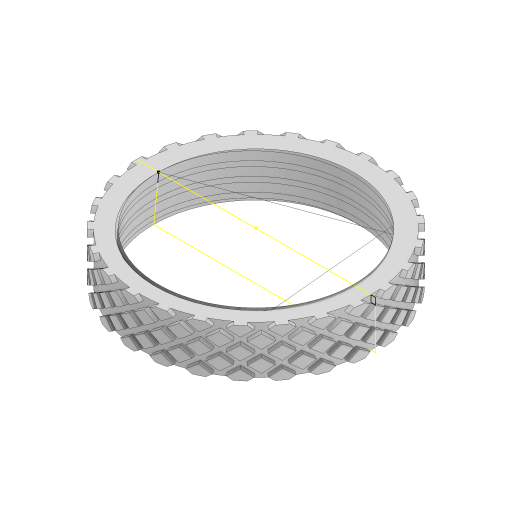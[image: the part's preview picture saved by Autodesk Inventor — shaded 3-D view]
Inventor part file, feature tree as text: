
AUTODESK INVENTOR PART (.ipt)
format: ipt  version: 2023 (Build 270158000, 158)  size: 1,646,592 bytes
history: native  units: mm
features: helix x6, sketch x4, pattern_circular x2, extrude x1, draft x1
ambient origin geometry x8: Origin, YZ Plane, XZ Plane, XY Plane, X Axis, Y Axis, Z Axis, Center Point
bodies: Solid1 (feature_tree)
feature tree (14):
  extrude  "Extrusion1"  Depth=6.52mm TaperAngle=0.0deg
  draft  "FaceDraft1"
  sketch  "Sketch2"  dims[d7=2.0mm d8=9.0mm d9=10.0mm d10=1.047198mm d11=90.0deg d12=90.0deg d13=0.0mm d14=0.0mm d15=2.0mm d16=3.0mm d17=10.0mm d18=-1.047198mm d19=90.0deg d20=90.0deg d21=0.0mm d22=0.0mm d23=3.0mm]
  sketch  "Sketch4"  dims[d52=70.0mm d53=9.0mm d54=10.0mm d55=0.0mm d56=90.0deg d57=90.0deg d58=0.0mm d59=0.0mm d60=70.0mm d61=9.0mm d62=10.0mm d63=0.0mm d64=90.0deg d65=90.0deg d66=0.0mm d67=0.0mm d68=250.0mm d69=360.0deg]
  helix  "Coil1"  [1 undecoded]
  helix  "Coil2"  [1 undecoded]
  sketch  "Sketch7"  dims[d71=70.0mm d72=9.0mm d73=10.0mm d74=0.0mm d75=90.0deg d76=90.0deg d77=0.0mm d78=0.0mm d79=70.0mm d80=9.0mm d81=10.0mm d82=0.0mm d83=90.0deg d84=90.0deg d85=0.0mm d86=0.0mm d87=250.0mm d88=360.0deg]
  helix  "Coil6"  [1 undecoded]
  helix  "Coil7"  [1 undecoded]
  pattern_circular  "Circular Pattern1"  [2 undecoded]
  helix  "Coil8"  [1 undecoded]
  helix  "Coil9"  [1 undecoded]
  pattern_circular  "Circular Pattern2"  [2 undecoded]
  sketch  "Sketch1"  dims[d0=26.5mm d2=6.52mm d3=0.0mm d4=1.047198mm]
note: 10 required parameter values undecoded (feature->parameter linkage not recoverable at this tier; creation-order binding heuristic only, values carry confidence <= 0.55)
